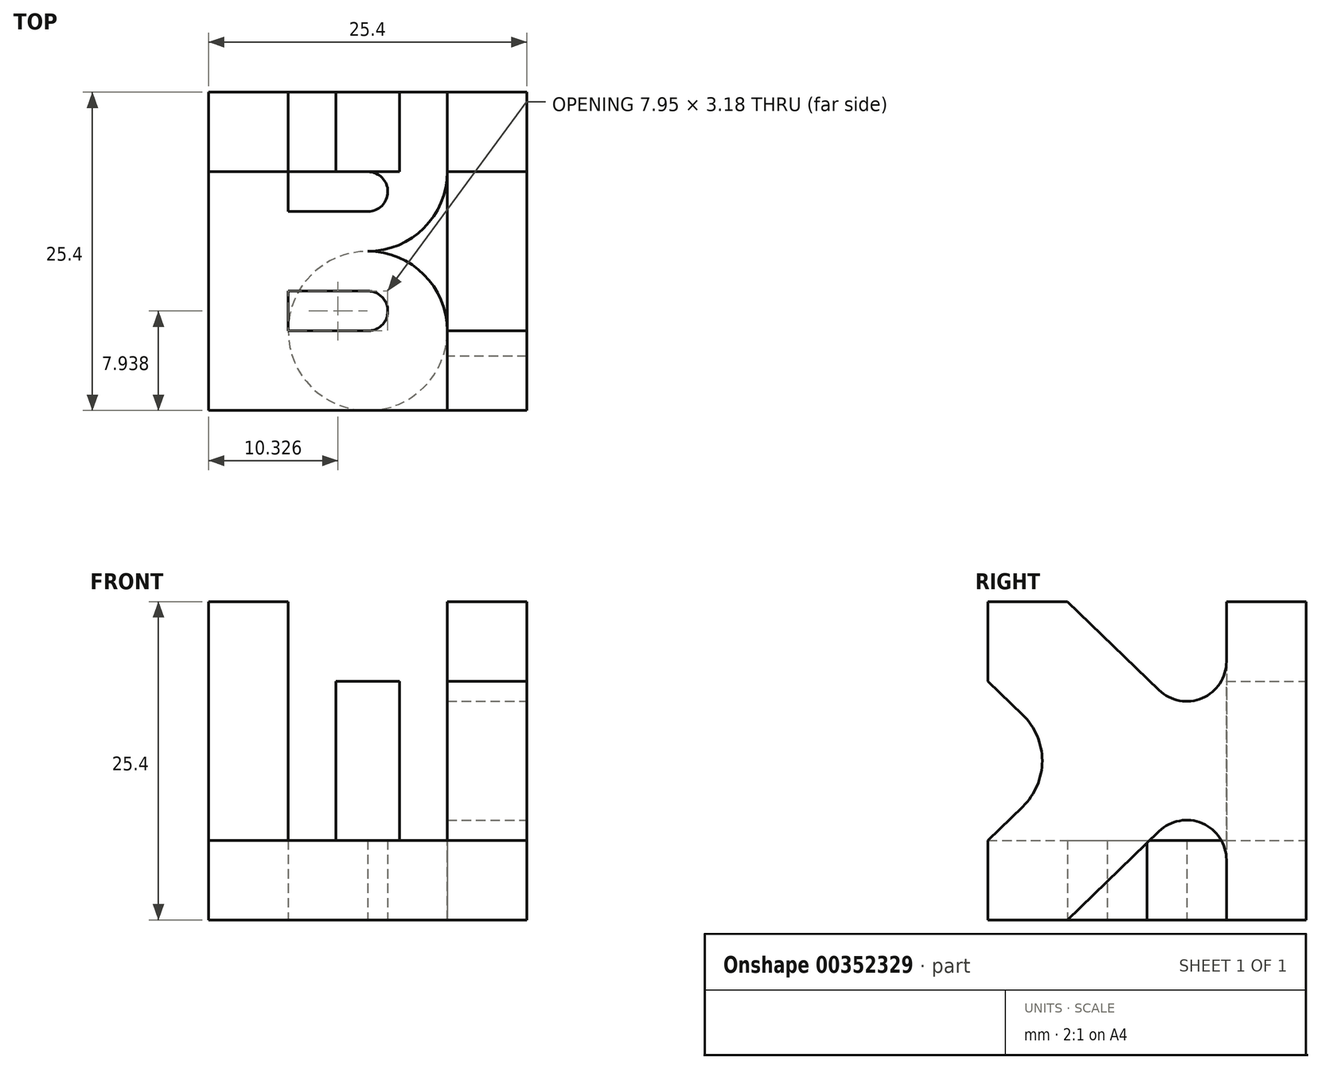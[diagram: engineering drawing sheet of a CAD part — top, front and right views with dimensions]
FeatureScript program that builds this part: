
annotation { "Feature Type Name" : "Feature", "Feature Type Description" : "" }
export const myFeature = defineFeature(function(context is Context, id is Id, definition is map)
    precondition{}
    {
        {
            var Q0;
            Q0=qCreatedBy(makeId("Front.planeOp"),FACE);
            cPlane(context, id + "F0", {"entities" : qUnion([Q0]), "cplaneType" : CPlaneType.OFFSET, "offset" : 25.4 * mm, "oppositeDirection" : true, "width" : 152.4 * mm, "height" : 152.4 * mm});
        }
        {
            var Q0;
            Q0=qCreatedBy(makeId("Right.planeOp"),FACE);
            cPlane(context, id + "F1", {"entities" : qUnion([Q0]), "cplaneType" : CPlaneType.OFFSET, "offset" : 25.4 * mm, "width" : 152.4 * mm, "height" : 152.4 * mm});
        }
        {
            var Q0;
            Q0=qCreatedBy(makeId("Top.planeOp"),FACE);
            var sketch = newSketch(context, id + "F2", { "sketchPlane" : qUnion([Q0])});
            skLineSegment(sketch, "E0", {"start": v(0, 0) * mm, "end": v(19.05, 0) * mm});
            skLineSegment(sketch, "E1", {"start": v(0, 0) * mm, "end": v(0, 25.4) * mm});
            skLineSegment(sketch, "E2", {"start": v(0, 25.4) * mm, "end": v(19.05, 25.4) * mm});
            skLineSegment(sketch, "E3", {"start": v(19.05, 25.4) * mm, "end": v(19.05, 19.05) * mm});
            skLineSegment(sketch, "E4", {"start": v(19.05, 0) * mm, "end": v(19.05, 6.35) * mm});
            skLineSegment(sketch, "E5", {"start": v(6.35, 19.05) * mm, "end": v(6.35, 15.87) * mm});
            skLineSegment(sketch, "E6", {"start": v(6.35, 19.05) * mm, "end": v(12.7, 19.05) * mm});
            skLineSegment(sketch, "E7", {"start": v(6.35, 15.87) * mm, "end": v(12.71, 15.87) * mm});
            skArc(sketch, "E8", {"start": v(19.05, 19.05) * mm, "mid": v(17.2, 14.56) * mm, "end": v(12.7, 12.7) * mm});
            skArc(sketch, "E9", {"start": v(12.71, 15.88) * mm, "mid": v(14.3, 17.47) * mm, "end": v(12.7, 19.05) * mm});
            skLineSegment(sketch, "E10", {"start": v(12.7, 12.7) * mm, "end": v(0, 12.7) * mm, "construction": true});
            skLineSegment(sketch, "E11.MirrorCS", {"start": v(6.35, 9.53) * mm, "end": v(12.71, 9.53) * mm});
            skLineSegment(sketch, "E12.MirrorCS", {"start": v(6.35, 6.35) * mm, "end": v(6.35, 9.53) * mm});
            skLineSegment(sketch, "E13.MirrorCS", {"start": v(6.35, 6.35) * mm, "end": v(12.7, 6.35) * mm});
            skArc(sketch, "E14.MirrorCS", {"start": v(12.71, 9.53) * mm, "mid": v(14.3, 7.93) * mm, "end": v(12.7, 6.35) * mm});
            skArc(sketch, "E15.MirrorCS", {"start": v(19.05, 6.35) * mm, "mid": v(17.2, 10.84) * mm, "end": v(12.7, 12.7) * mm});
            skSolve(sketch);
        }
        {
            var Q0;
            Q0=qCreatedBy(id+"F0.planeOp",FACE);
            var sketch = newSketch(context, id + "F3", { "sketchPlane" : qUnion([Q0])});
            skLineSegment(sketch, "E16", {"start": v(0, 25.4) * mm, "end": v(0, 0) * mm});
            skLineSegment(sketch, "E17", {"start": v(0, 0) * mm, "end": v(25.4, 0) * mm});
            skLineSegment(sketch, "E18", {"start": v(25.4, 0) * mm, "end": v(25.4, 25.4) * mm});
            skLineSegment(sketch, "E19", {"start": v(0, 25.4) * mm, "end": v(6.35, 25.4) * mm});
            skLineSegment(sketch, "E20", {"start": v(6.35, 25.4) * mm, "end": v(6.35, 6.35) * mm});
            skLineSegment(sketch, "E21", {"start": v(6.35, 6.35) * mm, "end": v(10.16, 6.35) * mm});
            skLineSegment(sketch, "E22", {"start": v(15.24, 6.35) * mm, "end": v(19.05, 6.35) * mm});
            skLineSegment(sketch, "E23", {"start": v(19.05, 6.35) * mm, "end": v(19.05, 25.4) * mm});
            skLineSegment(sketch, "E24", {"start": v(19.05, 25.4) * mm, "end": v(25.4, 25.4) * mm});
            skLineSegment(sketch, "E25", {"start": v(15.24, 6.35) * mm, "end": v(15.24, 19.05) * mm});
            skLineSegment(sketch, "E26", {"start": v(15.24, 19.05) * mm, "end": v(10.16, 19.05) * mm});
            skLineSegment(sketch, "E27", {"start": v(10.16, 19.05) * mm, "end": v(10.16, 6.35) * mm});
            skSolve(sketch);
        }
        {
            var Q0;
            Q0=qCreatedBy(id+"F1.planeOp",FACE);
            var sketch = newSketch(context, id + "F4", { "sketchPlane" : qUnion([Q0])});
            skLineSegment(sketch, "E28", {"start": v(25.4, 0) * mm, "end": v(25.4, 25.4) * mm});
            skLineSegment(sketch, "E29", {"start": v(25.4, 0) * mm, "end": v(19.05, 0) * mm});
            skLineSegment(sketch, "E30", {"start": v(6.35, 0) * mm, "end": v(0, 0) * mm});
            skLineSegment(sketch, "E31", {"start": v(0, 25.4) * mm, "end": v(6.35, 25.4) * mm});
            skLineSegment(sketch, "E32", {"start": v(19.05, 25.4) * mm, "end": v(25.4, 25.4) * mm});
            skLineSegment(sketch, "E33", {"start": v(0, 0) * mm, "end": v(0, 6.35) * mm});
            skLineSegment(sketch, "E34", {"start": v(0, 25.4) * mm, "end": v(0, 19.05) * mm});
            skLineSegment(sketch, "E35", {"start": v(19.05, 0) * mm, "end": v(19.05, 4.78) * mm});
            skLineSegment(sketch, "E36", {"start": v(13.67, 7.07) * mm, "end": v(6.35, 0) * mm});
            skLineSegment(sketch, "E37", {"start": v(0, 6.35) * mm, "end": v(6.57, 12.7) * mm});
            skLineSegment(sketch, "E38", {"start": v(6.57, 12.7) * mm, "end": v(0, 19.05) * mm});
            skLineSegment(sketch, "E39", {"start": v(6.35, 25.4) * mm, "end": v(13.67, 18.33) * mm});
            skLineSegment(sketch, "E40", {"start": v(19.05, 25.4) * mm, "end": v(19.05, 20.61) * mm});
            skPoint(sketch, "E41.visualSharp", {"position": v(19.05, 12.27) * mm});
            skArc(sketch, "E41.filletArc", {"start": v(19.05, 4.78) * mm, "mid": v(17.12, 7.7) * mm, "end": v(13.67, 7.07) * mm});
            skPoint(sketch, "E42.visualSharp", {"position": v(19.05, 13.13) * mm});
            skArc(sketch, "E42.filletArc", {"start": v(13.67, 18.33) * mm, "mid": v(17.12, 17.7) * mm, "end": v(19.05, 20.61) * mm});
            skSolve(sketch);
        }
        {
            var Q0;
            Q0=makeQuery(id+"F2.imprint","IMPRINT",FACE,{"disambiguationData":[TD([[makeQuery(id+"F2.imprint","IMPRINT",EDGE,{"derivedFrom":sQuery(id+"F2.wireOp",EDGE,"E0")}),1.0]])]});
            extrude(context, id + "F5", {"entities" : qUnion([Q0]), "depth" : 6.35 * mm});
        }
        {
            var Q0;
            Q0=makeQuery(id+"F4.imprint","IMPRINT",FACE,{"disambiguationData":[TD([[makeQuery(id+"F4.imprint","IMPRINT",EDGE,{"derivedFrom":sQuery(id+"F4.wireOp",EDGE,"E28")}),1.0]])]});
            extrude(context, id + "F6", {"entities" : qUnion([Q0]), "operationType" : NewBodyOperationType.ADD, "oppositeDirection" : true, "depth" : 6.35 * mm});
        }
        {
            var Q0;
            Q0=makeQuery(id+"F3.imprint","IMPRINT",FACE,{"disambiguationData":[TD([[makeQuery(id+"F3.imprint","IMPRINT",EDGE,{"derivedFrom":sQuery(id+"F3.wireOp",EDGE,"E16")}),1.0]])]});
            extrude(context, id + "F7", {"entities" : qUnion([Q0]), "operationType" : NewBodyOperationType.ADD, "depth" : 6.35 * mm});
        }
        {
            var Q0;
            Q0=makeQuery(id+"F6.opExtrude","SWEPT_EDGE",EDGE,{"disambiguationData":[OSD([sQuery(id+"F4.wireOp",EDGE,"E37"),sQuery(id+"F4.wireOp",EDGE,"E38")])]});
            fillet(context, id + "F8", {"entities" : qUnion([Q0]), "radius" : 5.08 * mm, "tangentPropagation" : true, "allowEdgeOverflow" : false});
        }
    });
